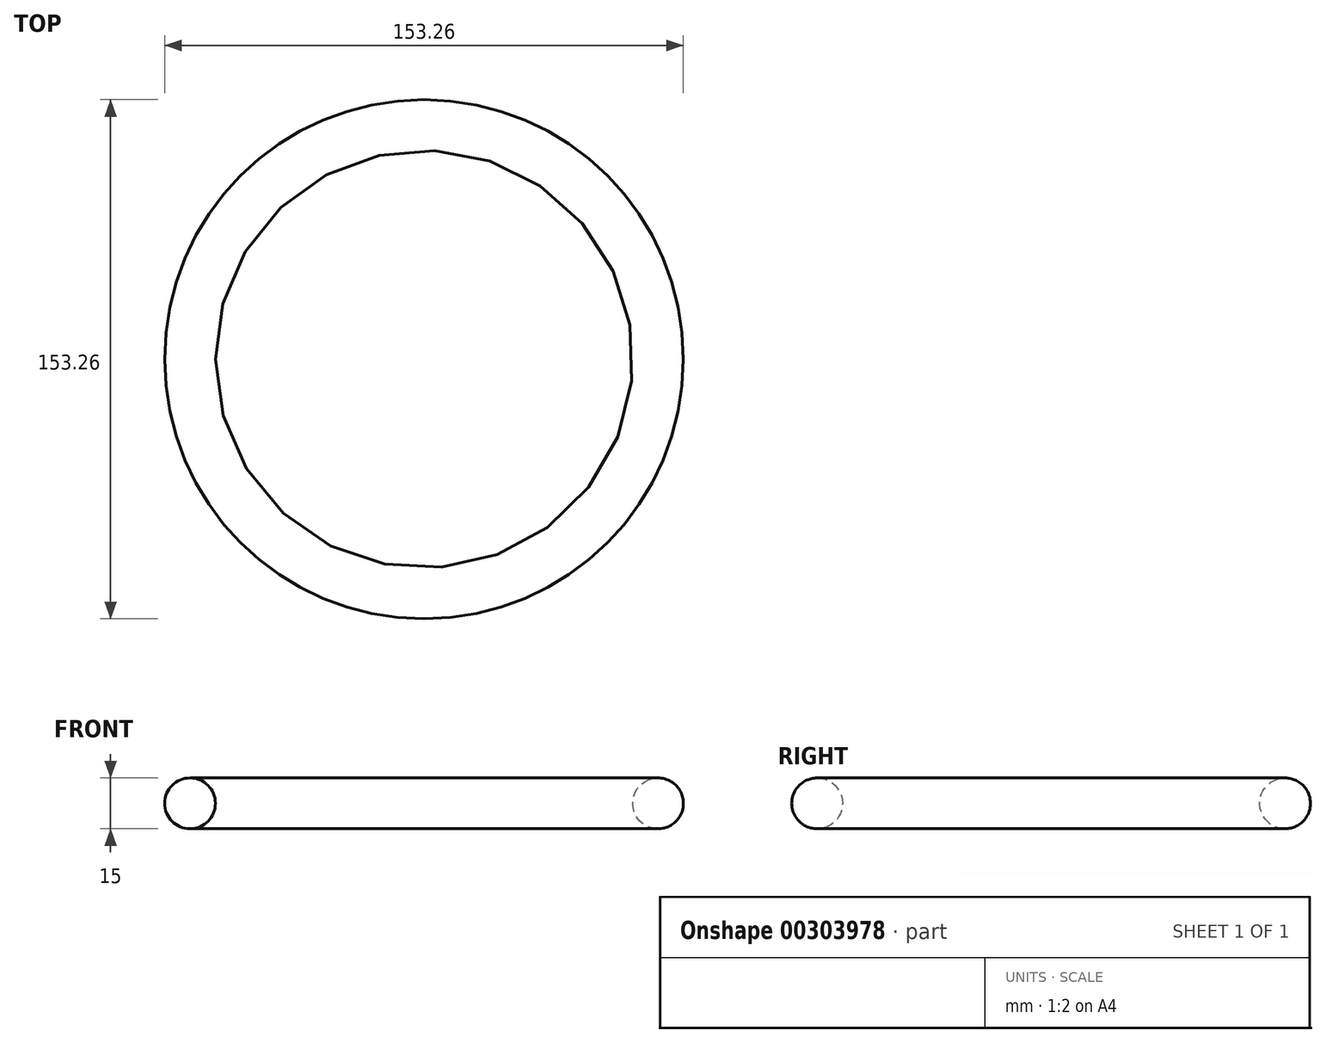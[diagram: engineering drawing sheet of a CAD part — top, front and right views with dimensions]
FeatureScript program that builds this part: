
annotation { "Feature Type Name" : "Feature", "Feature Type Description" : "" }
export const myFeature = defineFeature(function(context is Context, id is Id, definition is map)
    precondition{}
    {
        {
            var Q0;
            Q0=qCreatedBy(makeId("Right.planeOp"),FACE);
            var sketch = newSketch(context, id + "F0", { "sketchPlane" : qUnion([Q0])});
            skCircle(sketch, "E0", {"center": v(-69.13, 0) * mm, "radius": 7.5 * mm});
            skLineSegment(sketch, "E1", {"start": v(0, 0) * mm, "end": v(0, 42.88) * mm});
            skSolve(sketch);
        }
        {
            var Q0;
            Q0=makeQuery(id+"F0.imprint","IMPRINT",FACE,{"disambiguationData":[TD([[makeQuery(id+"F0.imprint","IMPRINT",EDGE,{"derivedFrom":sQuery(id+"F0.wireOp",EDGE,"E0")}),1.0]])]});
            var Q1;
            Q1=sQuery(id+"F0.wireOp",EDGE,"E1");
            revolve(context, id + "F1", {"entities" : qUnion([Q0]), "axis" : qUnion([Q1]), "revolveType" : RevolveType.FULL});
        }
    });
